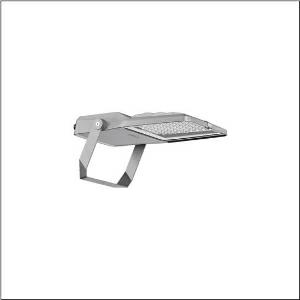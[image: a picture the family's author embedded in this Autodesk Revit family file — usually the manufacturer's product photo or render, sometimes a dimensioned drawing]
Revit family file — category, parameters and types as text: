
# Revit family: floodlight_fl_21_iq_mini___pl43_5xa7772d4a1a_cd74
name_source: partatom
category: Lighting Fixtures
units: mm (PartAtom-declared; Revit-internal decimal feet)

## family parameters
Cut with Voids When Loaded = No
Host = Face
Light Source = No
Part Type = Normal
Room Calculation Point = No
Round Connector Dimension = Use Diameter
Shared = No

## types (1)
- --- (1 x LED, 19090 lm, 143 W, 4000K)
    Apparent Load = 143 VA
    CIE Flux Codes = 27 78 99 100 100
    Color Rendering = 70
    Color Temperature = 4000K
    Default Elevation = 1800 mm
    Description = Floodlight FL 21 iQ mini, floodlight, primary light control with lens, of PMMA, primary optical cover: protective disc, of toughened safety glass, transparent, light distribution: PL43, light emission: direct distribution, installation type: surface-mounted, LED, High Power LED, rated luminous flux: 19.090lm, luminous efficacy: 134lm/W, light colour: 740, colour temperature: 4000K, control gear: iQ Street-Remote/DALI, control: Street-Remote, Auto-Match, Temp-Guard, Night-Set, Smart-Wire, Desk-Remote (wireless, voltage-free reading and setting of iQ features in the workshop via application-optimized NFC function/RFID function), optimised constant luminous flux control (CLO 2.0), with terminal, 6-pole, mains connection: 220..240V, AC, 50/60Hz, start of lifetime: 143W, end of service life: 152W, reduction: 61W, luminaire housing, of diecast aluminium, powder-coated, Siteco® metallic grey (DB 702S), corrosivity category C5 mid according to DIN EN ISO 12944, suitable for swimming pools, chlorine-resistant, sealing non-destructively replaceable, mounting bracket, of steel, galvanised, powder-coated, Siteco® metallic grey (DB 702S), protection rating (complete): IP66, insulation class (complete): insulation class II (safety insulation), certification: CE, ENEC, VDE, protection symbol: D, impact resistance: IK08, permissible operating ambient temperature: -40..+40°C, permissible operating ambient temperature for outdoor applications: -40..+50°C, standard: DIN EN 12944, LABS conformity tested according to VDMA 24364:2018-05, packaging unit: 1 piece

Light Distribution: PL43
    Height = 70 mm
    Lamp = 1 x LED
    Lamp Light Flux = 19090 lm
    Lamp Power = 143 W
    Lamp count = 1
    Length = 485 mm
    Luminous efficacy = 133 lm/W
    Manufacturer = Siteco
    ModVariant = No
    Model = 5XA7772D4A1A
    Number of Poles = 1
    OnlyDefault = Yes
    Power Factor = 1
    Product Name = Floodlight FL 21 iQ mini | PL43
    Product group = floodlight | pylon annexe
    ProductGroupID = 6200
    Protection Class = Protection class II
    Protection Degree = IP 66
    RLX_Detail_Level = 1
    RLX_Emergency_Light_Flux = 0 lm
    RLX_Emergency_Type = 0
    RLX_Emergency_Type_DB = No
    RlxData = <blob elided: 96613 chars, md5=07e567d9>
    Socket = socket
    Standby Power = 0 W
    System Light Flux = 19090 lm
    System Power = 143 W
    Type Comments = factory setting: luminous flux: 100 % | dim-lin: 254 | 730 mA
    Type Image = l_1006845.jpg
    URL = http://relux.com
    VarID = @adj_161360
    Voltage = 0 V
    Weight = 0.00 kg
    Width = 337 mm

## geometry (parser evidence)
native form markers: Blend x4, Sweep x12
no freeform markers — native parametric forms only
